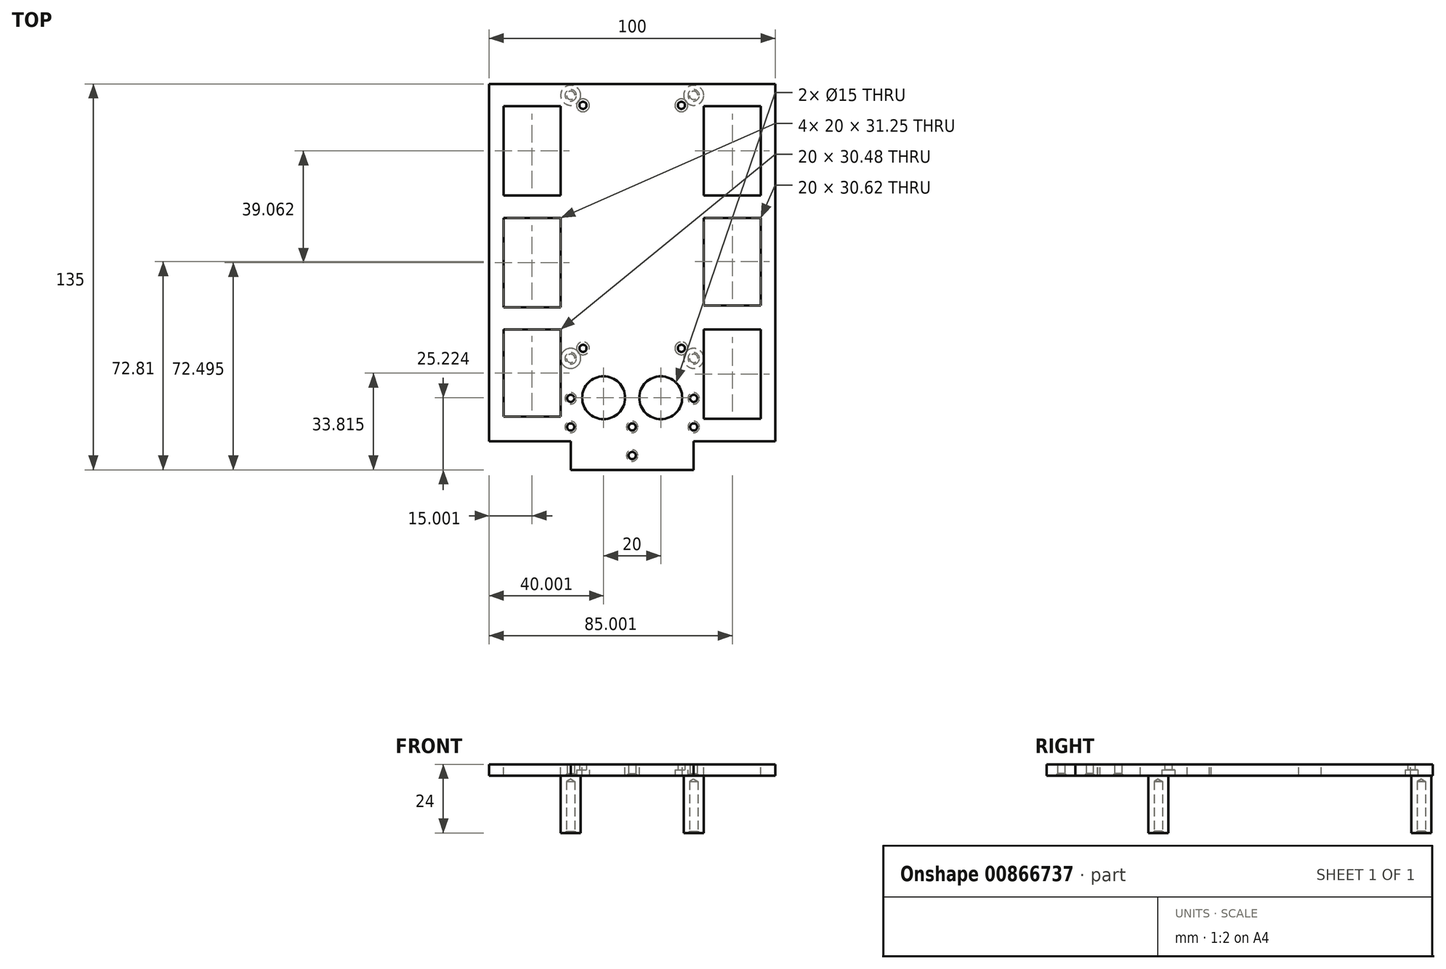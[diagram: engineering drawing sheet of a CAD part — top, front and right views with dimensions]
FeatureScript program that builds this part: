
annotation { "Feature Type Name" : "Feature", "Feature Type Description" : "" }
export const myFeature = defineFeature(function(context is Context, id is Id, definition is map)
    precondition{}
    {
        {
            assignVariable(context, id + "F0", {"name" : "RackThickness", "anyValue" : 4});
        }
        {
            assignVariable(context, id + "F1", {"name" : "PillarHeight", "anyValue" : 20});
        }
        {
            assignVariable(context, id + "F2", {"name" : "TailExtension", "anyValue" : 25});
        }
        {
            assignVariable(context, id + "F3", {"name" : "RackWidthExtension", "anyValue" : 25});
        }
        {
            var Q0;
            Q0=qCreatedBy(makeId("Top.planeOp"),FACE);
            var sketch = newSketch(context, id + "F4", { "sketchPlane" : qUnion([Q0])});
            skLineSegment(sketch, "E0.bottom", {"start": v(-22.43, 77.5) * mm, "end": v(27.57, 77.5) * mm});
            skLineSegment(sketch, "E0.top", {"start": v(-22.43, -22.5) * mm, "end": v(27.57, -22.5) * mm});
            skLineSegment(sketch, "E0.left", {"start": v(-22.43, 77.5) * mm, "end": v(-22.43, -22.5) * mm});
            skLineSegment(sketch, "E0.right", {"start": v(27.57, 77.5) * mm, "end": v(27.57, -22.5) * mm});
            skPoint(sketch, "E1", {"position": v(-14.63, 70) * mm});
            skPoint(sketch, "E2", {"position": v(19.77, 70) * mm});
            skPoint(sketch, "E3", {"position": v(19.77, -15) * mm});
            skPoint(sketch, "E4", {"position": v(-14.63, -15) * mm});
            skPoint(sketch, "E5", {"position": v(-18.93, -18.5) * mm});
            skPoint(sketch, "E6", {"position": v(24.07, -18.5) * mm});
            skPoint(sketch, "E7", {"position": v(24.07, 73.5) * mm});
            skPoint(sketch, "E8", {"position": v(-18.93, 73.5) * mm});
            skCircle(sketch, "E9", {"center": v(-18.93, 73.5) * mm, "radius": 3.5 * mm});
            skCircle(sketch, "E10", {"center": v(-18.93, -18.5) * mm, "radius": 3.5 * mm});
            skCircle(sketch, "E11", {"center": v(24.07, -18.5) * mm, "radius": 3.5 * mm});
            skCircle(sketch, "E12", {"center": v(24.07, 73.5) * mm, "radius": 3.5 * mm});
            skSolve(sketch);
        }
        {
            var Q0;
            Q0=makeQuery(id+"F4.imprint","IMPRINT",FACE,{"disambiguationData":[TD([[makeQuery(id+"F4.imprint","IMPRINT",EDGE,{"derivedFrom":sQuery(id+"F4.wireOp",EDGE,"E0.bottom")}),-1.0]])]});
            var Q1;
            Q1=makeQuery(id+"F4.imprint","IMPRINT",FACE,{"disambiguationData":[TD([[makeQuery(id+"F4.imprint","IMPRINT",EDGE,{"derivedFrom":sQuery(id+"F4.wireOp",EDGE,"E10")}),1.0]])]});
            var Q2;
            Q2=makeQuery(id+"F4.imprint","IMPRINT",FACE,{"disambiguationData":[TD([[makeQuery(id+"F4.imprint","IMPRINT",EDGE,{"derivedFrom":sQuery(id+"F4.wireOp",EDGE,"E11")}),1.0]])]});
            var Q3;
            Q3=makeQuery(id+"F4.imprint","IMPRINT",FACE,{"disambiguationData":[TD([[makeQuery(id+"F4.imprint","IMPRINT",EDGE,{"derivedFrom":sQuery(id+"F4.wireOp",EDGE,"E9")}),1.0]])]});
            var Q4;
            Q4=makeQuery(id+"F4.imprint","IMPRINT",FACE,{"disambiguationData":[TD([[makeQuery(id+"F4.imprint","IMPRINT",EDGE,{"derivedFrom":sQuery(id+"F4.wireOp",EDGE,"E12")}),1.0]])]});
            extrude(context, id + "F5", {"entities" : qUnion([Q0, Q1, Q2, Q3, Q4]), "depth" : (getVariable(context, 'RackThickness')) * mm, "offsetDistance" : 25 * mm});
        }
        {
            var Q0;
            Q0=sQuery(id+"F4.wireOp",VERTEX,"E2");
            var Q1;
            Q1=sQuery(id+"F4.wireOp",VERTEX,"E3");
            var Q2;
            Q2=sQuery(id+"F4.wireOp",VERTEX,"E4");
            var Q3;
            Q3=sQuery(id+"F4.wireOp",VERTEX,"E1");
            var Q4;
            Q4=makeQuery(id+"F5.opExtrude","SWEPT_BODY",BODY,{"disambiguationData":[OSD([sQuery(id+"F4.wireOp",EDGE,"E0.bottom"),sQuery(id+"F4.wireOp",EDGE,"E0.top"),sQuery(id+"F4.wireOp",EDGE,"E0.left"),sQuery(id+"F4.wireOp",EDGE,"E0.right")])]});
            hole(context, id + "F6", {"style" : HoleStyle.C_BORE, "endStyle" : HoleEndStyle.THROUGH, "oppositeDirection" : true, "holeDiameter" : 2.5 * mm, "cBoreDiameter" : 4.5 * mm, "cBoreDepth" : 2 * mm, "majorDiameter" : 5 * mm, "isTappedThrough" : true, "tappedDepth" : 12 * mm, "tapClearance" : 3, "startFromSketch" : true, "locations" : qUnion([Q0, Q1, Q2, Q3]), "scope" : qUnion([Q4])});
        }
        {
            var Q0;
            Q0=makeQuery(id+"F4.imprint","IMPRINT",FACE,{"disambiguationData":[TD([[makeQuery(id+"F4.imprint","IMPRINT",EDGE,{"derivedFrom":sQuery(id+"F4.wireOp",EDGE,"E10")}),1.0]])]});
            var Q1;
            Q1=makeQuery(id+"F4.imprint","IMPRINT",FACE,{"disambiguationData":[TD([[makeQuery(id+"F4.imprint","IMPRINT",EDGE,{"derivedFrom":sQuery(id+"F4.wireOp",EDGE,"E11")}),1.0]])]});
            var Q2;
            Q2=makeQuery(id+"F4.imprint","IMPRINT",FACE,{"disambiguationData":[TD([[makeQuery(id+"F4.imprint","IMPRINT",EDGE,{"derivedFrom":sQuery(id+"F4.wireOp",EDGE,"E9")}),1.0]])]});
            var Q3;
            Q3=makeQuery(id+"F4.imprint","IMPRINT",FACE,{"disambiguationData":[TD([[makeQuery(id+"F4.imprint","IMPRINT",EDGE,{"derivedFrom":sQuery(id+"F4.wireOp",EDGE,"E12")}),1.0]])]});
            extrude(context, id + "F7", {"entities" : qUnion([Q0, Q1, Q2, Q3]), "operationType" : NewBodyOperationType.ADD, "oppositeDirection" : true, "depth" : (getVariable(context, 'PillarHeight')) * mm, "offsetDistance" : 25 * mm});
        }
        {
            var Q0;
            Q0=makeQuery(id+"F7.opExtrude","CAP_FACE",FACE,{"disambiguationData":[OSD([sQuery(id+"F4.wireOp",EDGE,"E9")])],"isStart":false});
            var sketch = newSketch(context, id + "F8", { "sketchPlane" : qUnion([Q0])});
            skPoint(sketch, "E13", {"position": v(-18.93, -73.5) * mm});
            skSolve(sketch);
        }
        {
            var Q0;
            Q0=sQuery(id+"F8.wireOp",VERTEX,"E13");
            var Q1;
            Q1=makeQuery(id+"F5.opExtrude","SWEPT_BODY",BODY,{"disambiguationData":[OSD([sQuery(id+"F4.wireOp",EDGE,"E0.bottom"),sQuery(id+"F4.wireOp",EDGE,"E0.top"),sQuery(id+"F4.wireOp",EDGE,"E0.left"),sQuery(id+"F4.wireOp",EDGE,"E0.right")])]});
            hole(context, id + "F9", {"style" : HoleStyle.C_SINK, "endStyle" : HoleEndStyle.BLIND, "holeDiameter" : 2.9 * mm, "cSinkDiameter" : 4 * mm, "cSinkAngle" : 90 * degree, "majorDiameter" : 5 * mm, "holeDepth" : (.9 * getVariable(context, 'PillarHeight')) * mm, "isTappedThrough" : true, "tappedDepth" : 12 * mm, "tapClearance" : 3, "startFromSketch" : true, "locations" : qUnion([Q0]), "scope" : qUnion([Q1])});
        }
        {
            var Q0;
            Q0=makeQuery(id+"F7.opExtrude","CAP_FACE",FACE,{"disambiguationData":[OSD([sQuery(id+"F4.wireOp",EDGE,"E10")])],"isStart":false});
            var sketch = newSketch(context, id + "F10", { "sketchPlane" : qUnion([Q0])});
            skPoint(sketch, "E14", {"position": v(-18.93, 18.5) * mm});
            skSolve(sketch);
        }
        {
            var Q0;
            Q0=sQuery(id+"F10.wireOp",VERTEX,"E14");
            var Q1;
            Q1=makeQuery(id+"F5.opExtrude","SWEPT_BODY",BODY,{"disambiguationData":[OSD([sQuery(id+"F4.wireOp",EDGE,"E0.bottom"),sQuery(id+"F4.wireOp",EDGE,"E0.top"),sQuery(id+"F4.wireOp",EDGE,"E0.left"),sQuery(id+"F4.wireOp",EDGE,"E0.right")])]});
            hole(context, id + "F11", {"style" : HoleStyle.C_SINK, "endStyle" : HoleEndStyle.BLIND, "holeDiameter" : 2.9 * mm, "cSinkDiameter" : 4 * mm, "cSinkAngle" : 90 * degree, "majorDiameter" : 5 * mm, "holeDepth" : (.9 * getVariable(context, 'PillarHeight')) * mm, "isTappedThrough" : true, "tappedDepth" : 12 * mm, "tapClearance" : 3, "startFromSketch" : true, "locations" : qUnion([Q0]), "scope" : qUnion([Q1])});
        }
        {
            var Q0;
            Q0=makeQuery(id+"F7.opExtrude","CAP_FACE",FACE,{"disambiguationData":[OSD([sQuery(id+"F4.wireOp",EDGE,"E12")])],"isStart":false});
            var sketch = newSketch(context, id + "F12", { "sketchPlane" : qUnion([Q0])});
            skPoint(sketch, "E15", {"position": v(24.07, -73.5) * mm});
            skSolve(sketch);
        }
        {
            var Q0;
            Q0=sQuery(id+"F12.wireOp",VERTEX,"E15");
            var Q1;
            Q1=makeQuery(id+"F5.opExtrude","SWEPT_BODY",BODY,{"disambiguationData":[OSD([sQuery(id+"F4.wireOp",EDGE,"E0.bottom"),sQuery(id+"F4.wireOp",EDGE,"E0.top"),sQuery(id+"F4.wireOp",EDGE,"E0.left"),sQuery(id+"F4.wireOp",EDGE,"E0.right")])]});
            hole(context, id + "F13", {"style" : HoleStyle.C_SINK, "endStyle" : HoleEndStyle.BLIND, "holeDiameter" : 2.9 * mm, "cSinkDiameter" : 4 * mm, "cSinkAngle" : 90 * degree, "majorDiameter" : 5 * mm, "holeDepth" : (.9 * getVariable(context, 'PillarHeight')) * mm, "isTappedThrough" : true, "tappedDepth" : 12 * mm, "tapClearance" : 3, "startFromSketch" : true, "locations" : qUnion([Q0]), "scope" : qUnion([Q1])});
        }
        {
            var Q0;
            Q0=makeQuery(id+"F7.opExtrude","CAP_FACE",FACE,{"disambiguationData":[OSD([sQuery(id+"F4.wireOp",EDGE,"E11")])],"isStart":false});
            var sketch = newSketch(context, id + "F14", { "sketchPlane" : qUnion([Q0])});
            skPoint(sketch, "E16", {"position": v(24.07, 18.5) * mm});
            skSolve(sketch);
        }
        {
            var Q0;
            Q0=sQuery(id+"F14.wireOp",VERTEX,"E16");
            var Q1;
            Q1=makeQuery(id+"F5.opExtrude","SWEPT_BODY",BODY,{"disambiguationData":[OSD([sQuery(id+"F4.wireOp",EDGE,"E0.bottom"),sQuery(id+"F4.wireOp",EDGE,"E0.top"),sQuery(id+"F4.wireOp",EDGE,"E0.left"),sQuery(id+"F4.wireOp",EDGE,"E0.right")])]});
            hole(context, id + "F15", {"style" : HoleStyle.C_SINK, "endStyle" : HoleEndStyle.BLIND, "holeDiameter" : 2.9 * mm, "cSinkDiameter" : 4 * mm, "cSinkAngle" : 90 * degree, "majorDiameter" : 5 * mm, "holeDepth" : (.9 * getVariable(context, 'PillarHeight')) * mm, "isTappedThrough" : true, "tappedDepth" : 12 * mm, "tapClearance" : 3, "startFromSketch" : true, "locations" : qUnion([Q0]), "scope" : qUnion([Q1])});
        }
        {
            var Q0;
            Q0=makeQuery(id+"F5.opExtrude","SWEPT_FACE",FACE,{"disambiguationData":[OSD([sQuery(id+"F4.wireOp",EDGE,"E0.top")])]});
            extrude(context, id + "F16", {"entities" : qUnion([Q0]), "operationType" : NewBodyOperationType.ADD, "depth" : (getVariable(context, 'TailExtension')) * mm, "offsetDistance" : 25 * mm});
        }
        {
            var Q0;
            {var subQ0=sQuery(id+"F4.wireOp",EDGE,"E0.top");Q0=makeQuery(id+"F16.boolean.opBoolean","MERGE",FACE,{"derivedFrom":[makeQuery(id+"F5.opExtrude","CAP_FACE",FACE,{"disambiguationData":[OSD([sQuery(id+"F4.wireOp",EDGE,"E0.bottom"),subQ0,sQuery(id+"F4.wireOp",EDGE,"E0.left"),sQuery(id+"F4.wireOp",EDGE,"E0.right")])],"isStart":false}),makeQuery(id+"F16.opExtrude","SWEPT_FACE",FACE,{"disambiguationData":[OSD([subQ0]),TDD([makeQuery(id+"F5.opExtrude","CAP_EDGE",EDGE,{"disambiguationData":[OSD([subQ0])],"isStart":false})])]})]});}
            var sketch = newSketch(context, id + "F17", { "sketchPlane" : qUnion([Q0])});
            skLineSegment(sketch, "E17.bottom", {"start": v(22.57, -42.5) * mm, "end": v(-17.43, -42.5) * mm});
            skLineSegment(sketch, "E17.top", {"start": v(22.57, -22.05) * mm, "end": v(-17.43, -22.05) * mm});
            skLineSegment(sketch, "E17.left", {"start": v(22.57, -42.5) * mm, "end": v(22.57, -22.05) * mm});
            skLineSegment(sketch, "E17.right", {"start": v(-17.43, -42.5) * mm, "end": v(-17.43, -22.05) * mm});
            skPoint(sketch, "E18", {"position": v(2.57, -47.5) * mm});
            skPoint(sketch, "E19", {"position": v(2.57, -42.5) * mm});
            skLineSegment(sketch, "E20", {"start": v(2.57, -47.5) * mm, "end": v(2.57, -42.5) * mm});
            skPoint(sketch, "E21", {"position": v(2.57, -45) * mm});
            skCircle(sketch, "E22", {"center": v(2.57, -45) * mm, "radius": 1.25 * mm});
            skPoint(sketch, "E23", {"position": v(2.57, -22.05) * mm});
            skLineSegment(sketch, "E24", {"start": v(2.57, -22.05) * mm, "end": v(2.57, -42.5) * mm, "construction": true});
            skPoint(sketch, "E25", {"position": v(2.57, -32.28) * mm});
            skPoint(sketch, "E26", {"position": v(22.57, -32.28) * mm});
            skPoint(sketch, "E27", {"position": v(-17.43, -32.28) * mm});
            skLineSegment(sketch, "E28", {"start": v(22.57, -32.28) * mm, "end": v(2.57, -32.28) * mm, "construction": true});
            skPoint(sketch, "E29", {"position": v(12.57, -32.28) * mm});
            skLineSegment(sketch, "E30", {"start": v(2.57, -32.28) * mm, "end": v(-17.43, -32.28) * mm, "construction": true});
            skPoint(sketch, "E31", {"position": v(-7.43, -32.28) * mm});
            skCircle(sketch, "E32", {"center": v(12.57, -32.28) * mm, "radius": 7.5 * mm});
            skCircle(sketch, "E33", {"center": v(-7.43, -32.28) * mm, "radius": 7.5 * mm});
            skSolve(sketch);
        }
        {
            var Q0;
            {var subQ0=sQuery(id+"F4.wireOp",EDGE,"E0.right");Q0=makeQuery(id+"F16.boolean.opBoolean","MERGE",FACE,{"derivedFrom":[makeQuery(id+"F5.opExtrude","SWEPT_FACE",FACE,{"disambiguationData":[OSD([subQ0])]}),makeQuery(id+"F16.opExtrude","SWEPT_FACE",FACE,{"disambiguationData":[OSD([sQuery(id+"F4.wireOp",EDGE,"E0.top"),subQ0])]})]});}
            extrude(context, id + "F18", {"entities" : qUnion([Q0]), "operationType" : NewBodyOperationType.ADD, "depth" : (getVariable(context, 'RackWidthExtension')) * mm, "offsetDistance" : 25 * mm});
        }
        {
            var Q0;
            {var subQ0=sQuery(id+"F4.wireOp",EDGE,"E0.left");Q0=makeQuery(id+"F16.boolean.opBoolean","MERGE",FACE,{"derivedFrom":[makeQuery(id+"F5.opExtrude","SWEPT_FACE",FACE,{"disambiguationData":[OSD([subQ0])]}),makeQuery(id+"F16.opExtrude","SWEPT_FACE",FACE,{"disambiguationData":[OSD([sQuery(id+"F4.wireOp",EDGE,"E0.top"),subQ0])]})]});}
            extrude(context, id + "F19", {"entities" : qUnion([Q0]), "operationType" : NewBodyOperationType.ADD, "depth" : (getVariable(context, 'RackWidthExtension')) * mm, "offsetDistance" : 25 * mm});
        }
        {
            var Q0;
            {var subQ0=sQuery(id+"F4.wireOp",EDGE,"E0.left");var subQ1=sQuery(id+"F4.wireOp",EDGE,"E0.top");var subQ2=sQuery(id+"F4.wireOp",EDGE,"E0.right");Q0=makeQuery(id+"F19.boolean.opBoolean","MERGE",FACE,{"derivedFrom":[makeQuery(id+"F18.boolean.opBoolean","MERGE",FACE,{"derivedFrom":[makeQuery(id+"F16.boolean.opBoolean","MERGE",FACE,{"derivedFrom":[makeQuery(id+"F5.opExtrude","CAP_FACE",FACE,{"disambiguationData":[OSD([sQuery(id+"F4.wireOp",EDGE,"E0.bottom"),subQ1,subQ0,subQ2])],"isStart":false}),makeQuery(id+"F16.opExtrude","SWEPT_FACE",FACE,{"disambiguationData":[OSD([subQ1]),TDD([makeQuery(id+"F5.opExtrude","CAP_EDGE",EDGE,{"disambiguationData":[OSD([subQ1])],"isStart":false})])]})]}),makeQuery(id+"F18.opExtrude","SWEPT_FACE",FACE,{"disambiguationData":[OSD([subQ1,subQ2]),TDD([makeQuery(id+"F16.boolean.opBoolean","MERGE",EDGE,{"derivedFrom":[makeQuery(id+"F5.opExtrude","CAP_EDGE",EDGE,{"disambiguationData":[OSD([subQ2])],"isStart":false}),makeQuery(id+"F16.opExtrude","SWEPT_EDGE",EDGE,{"disambiguationData":[OSD([subQ1,subQ2]),TDD([makeQuery(id+"F5.opExtrude","CAP_VERTEX",VERTEX,{"disambiguationData":[OSD([subQ1,subQ2])],"isStart":false})])]})]})])]})]}),makeQuery(id+"F19.opExtrude","SWEPT_FACE",FACE,{"disambiguationData":[OSD([subQ1,subQ0]),TDD([makeQuery(id+"F16.boolean.opBoolean","MERGE",EDGE,{"derivedFrom":[makeQuery(id+"F5.opExtrude","CAP_EDGE",EDGE,{"disambiguationData":[OSD([subQ0])],"isStart":false}),makeQuery(id+"F16.opExtrude","SWEPT_EDGE",EDGE,{"disambiguationData":[OSD([subQ1,subQ0]),TDD([makeQuery(id+"F5.opExtrude","CAP_VERTEX",VERTEX,{"disambiguationData":[OSD([subQ1,subQ0])],"isStart":false})])]})]})])]})]});}
            var sketch = newSketch(context, id + "F20", { "sketchPlane" : qUnion([Q0])});
            skLineSegment(sketch, "E34.bottom", {"start": v(-42.43, 69.68) * mm, "end": v(-22.43, 69.68) * mm});
            skLineSegment(sketch, "E34.top", {"start": v(-42.43, 38.43) * mm, "end": v(-22.43, 38.43) * mm});
            skLineSegment(sketch, "E34.left", {"start": v(-42.43, 69.68) * mm, "end": v(-42.43, 38.43) * mm});
            skLineSegment(sketch, "E34.right", {"start": v(-22.43, 69.68) * mm, "end": v(-22.43, 38.43) * mm});
            skLineSegment(sketch, "E35.bottom", {"start": v(-42.43, 30.62) * mm, "end": v(-22.43, 30.62) * mm});
            skLineSegment(sketch, "E35.top", {"start": v(-42.43, -0.63) * mm, "end": v(-22.43, -0.63) * mm});
            skLineSegment(sketch, "E35.left", {"start": v(-42.43, 30.62) * mm, "end": v(-42.43, -0.63) * mm});
            skLineSegment(sketch, "E35.right", {"start": v(-22.43, 30.62) * mm, "end": v(-22.43, -0.63) * mm});
            skLineSegment(sketch, "E36.bottom", {"start": v(-42.43, -8.44) * mm, "end": v(-22.43, -8.44) * mm});
            skLineSegment(sketch, "E36.top", {"start": v(-42.43, -38.93) * mm, "end": v(-22.43, -38.93) * mm});
            skLineSegment(sketch, "E36.left", {"start": v(-42.43, -8.44) * mm, "end": v(-42.43, -38.93) * mm});
            skLineSegment(sketch, "E36.right", {"start": v(-22.43, -8.44) * mm, "end": v(-22.43, -38.93) * mm});
            skLineSegment(sketch, "E37.bottom", {"start": v(47.57, 69.68) * mm, "end": v(27.57, 69.68) * mm});
            skLineSegment(sketch, "E37.top", {"start": v(47.57, 38.43) * mm, "end": v(27.57, 38.43) * mm});
            skLineSegment(sketch, "E37.left", {"start": v(47.57, 69.68) * mm, "end": v(47.57, 38.43) * mm});
            skLineSegment(sketch, "E37.right", {"start": v(27.57, 69.68) * mm, "end": v(27.57, 38.43) * mm});
            skLineSegment(sketch, "E38.bottom", {"start": v(27.57, 30.62) * mm, "end": v(47.57, 30.62) * mm});
            skLineSegment(sketch, "E38.top", {"start": v(27.57, 0) * mm, "end": v(47.57, 0) * mm});
            skLineSegment(sketch, "E38.left", {"start": v(27.57, 30.62) * mm, "end": v(27.57, 0) * mm});
            skLineSegment(sketch, "E38.right", {"start": v(47.57, 30.62) * mm, "end": v(47.57, 0) * mm});
            skLineSegment(sketch, "E39.bottom", {"start": v(27.57, -8.44) * mm, "end": v(47.57, -8.44) * mm});
            skLineSegment(sketch, "E39.top", {"start": v(27.57, -39.7) * mm, "end": v(47.57, -39.7) * mm});
            skLineSegment(sketch, "E39.left", {"start": v(27.57, -8.44) * mm, "end": v(27.57, -39.7) * mm});
            skLineSegment(sketch, "E39.right", {"start": v(47.57, -8.44) * mm, "end": v(47.57, -39.7) * mm});
            skSolve(sketch);
        }
        {
            var Q0;
            Q0=makeQuery(id+"F20.imprint","IMPRINT",FACE,{"disambiguationData":[TD([[makeQuery(id+"F20.imprint","IMPRINT",EDGE,{"derivedFrom":sQuery(id+"F20.wireOp",EDGE,"E36.bottom")}),-1.0]])]});
            var Q1;
            Q1=makeQuery(id+"F20.imprint","IMPRINT",FACE,{"disambiguationData":[TD([[makeQuery(id+"F20.imprint","IMPRINT",EDGE,{"derivedFrom":sQuery(id+"F20.wireOp",EDGE,"E35.bottom")}),-1.0]])]});
            var Q2;
            Q2=makeQuery(id+"F20.imprint","IMPRINT",FACE,{"disambiguationData":[TD([[makeQuery(id+"F20.imprint","IMPRINT",EDGE,{"derivedFrom":sQuery(id+"F20.wireOp",EDGE,"E34.bottom")}),-1.0]])]});
            var Q3;
            Q3=makeQuery(id+"F20.imprint","IMPRINT",FACE,{"disambiguationData":[TD([[makeQuery(id+"F20.imprint","IMPRINT",EDGE,{"derivedFrom":sQuery(id+"F20.wireOp",EDGE,"E37.bottom")}),1.0]])]});
            var Q4;
            Q4=makeQuery(id+"F20.imprint","IMPRINT",FACE,{"disambiguationData":[TD([[makeQuery(id+"F20.imprint","IMPRINT",EDGE,{"derivedFrom":sQuery(id+"F20.wireOp",EDGE,"E38.bottom")}),-1.0]])]});
            var Q5;
            Q5=makeQuery(id+"F20.imprint","IMPRINT",FACE,{"disambiguationData":[TD([[makeQuery(id+"F20.imprint","IMPRINT",EDGE,{"derivedFrom":sQuery(id+"F20.wireOp",EDGE,"E39.bottom")}),-1.0]])]});
            extrude(context, id + "F21", {"entities" : qUnion([Q0, Q1, Q2, Q3, Q4, Q5]), "operationType" : NewBodyOperationType.REMOVE, "oppositeDirection" : true, "depth" : (getVariable(context, 'RackThickness')) * mm, "offsetDistance" : 25 * mm});
        }
        {
            var Q0;
            Q0=makeQuery(id+"F17.imprint","IMPRINT",FACE,{"disambiguationData":[TD([[makeQuery(id+"F17.imprint","IMPRINT",EDGE,{"derivedFrom":sQuery(id+"F17.wireOp",EDGE,"E33")}),1.0]])]});
            var Q1;
            Q1=makeQuery(id+"F17.imprint","IMPRINT",FACE,{"disambiguationData":[TD([[makeQuery(id+"F17.imprint","IMPRINT",EDGE,{"derivedFrom":sQuery(id+"F17.wireOp",EDGE,"E32")}),1.0]])]});
            extrude(context, id + "F22", {"entities" : qUnion([Q0, Q1]), "operationType" : NewBodyOperationType.REMOVE, "oppositeDirection" : true, "depth" : (getVariable(context, 'RackThickness')) * mm, "offsetDistance" : 25 * mm});
        }
        {
            var Q0;
            {var subQ0=sQuery(id+"F4.wireOp",EDGE,"E0.left");var subQ1=sQuery(id+"F4.wireOp",EDGE,"E0.top");var subQ2=sQuery(id+"F4.wireOp",EDGE,"E0.right");Q0=makeQuery(id+"F19.boolean.opBoolean","MERGE",FACE,{"derivedFrom":[makeQuery(id+"F18.boolean.opBoolean","MERGE",FACE,{"derivedFrom":[makeQuery(id+"F16.opExtrude","CAP_FACE",FACE,{"disambiguationData":[OSD([subQ1])],"isStart":false}),makeQuery(id+"F18.opExtrude","SWEPT_FACE",FACE,{"disambiguationData":[OSD([subQ1,subQ2]),TDD([makeQuery(id+"F16.opExtrude","CAP_EDGE",EDGE,{"disambiguationData":[OSD([subQ1,subQ2])],"isStart":false})])]})]}),makeQuery(id+"F19.opExtrude","SWEPT_FACE",FACE,{"disambiguationData":[OSD([subQ1,subQ0]),TDD([makeQuery(id+"F16.opExtrude","CAP_EDGE",EDGE,{"disambiguationData":[OSD([subQ1,subQ0])],"isStart":false})])]})]});}
            var sketch = newSketch(context, id + "F23", { "sketchPlane" : qUnion([Q0])});
            skPoint(sketch, "E40", {"position": v(2.57, 4) * mm});
            skPoint(sketch, "E41", {"position": v(2.57, 0) * mm});
            skLineSegment(sketch, "E42", {"start": v(2.57, 4) * mm, "end": v(2.57, 0) * mm, "construction": true});
            skPoint(sketch, "E43", {"position": v(2.57, 2) * mm});
            skLineSegment(sketch, "E44.bottom", {"start": v(24.07, 0) * mm, "end": v(-18.93, 0) * mm, "construction": true});
            skLineSegment(sketch, "E44.top", {"start": v(24.07, 4) * mm, "end": v(-18.93, 4) * mm, "construction": true});
            skLineSegment(sketch, "E44.left", {"start": v(24.07, 0) * mm, "end": v(24.07, 4) * mm, "construction": true});
            skLineSegment(sketch, "E44.right", {"start": v(-18.93, 0) * mm, "end": v(-18.93, 4) * mm, "construction": true});
            skLineSegment(sketch, "E45.bottom", {"start": v(24.07, 4) * mm, "end": v(-18.93, 4) * mm});
            skLineSegment(sketch, "E45.top", {"start": v(24.07, 0) * mm, "end": v(-18.93, 0) * mm});
            skLineSegment(sketch, "E45.left", {"start": v(24.07, 4) * mm, "end": v(24.07, 0) * mm});
            skLineSegment(sketch, "E45.right", {"start": v(-18.93, 4) * mm, "end": v(-18.93, 0) * mm});
            skSolve(sketch);
        }
        {
            var Q0;
            Q0=makeQuery(id+"F23.imprint","IMPRINT",FACE,{"disambiguationData":[TD([[makeQuery(id+"F23.imprint","IMPRINT",EDGE,{"derivedFrom":sQuery(id+"F23.wireOp",EDGE,"E45.bottom")}),-1.0]])]});
            extrude(context, id + "F24", {"entities" : qUnion([Q0]), "operationType" : NewBodyOperationType.ADD, "depth" : 10 * mm, "offsetDistance" : 25 * mm});
        }
        {
            var Q0;
            {var subQ0=sQuery(id+"F4.wireOp",EDGE,"E0.left");var subQ1=sQuery(id+"F4.wireOp",EDGE,"E0.top");var subQ2=sQuery(id+"F4.wireOp",EDGE,"E0.right");var subQ3=sQuery(id+"F4.wireOp",EDGE,"E0.bottom");var subQ4=makeQuery(id+"F5.opExtrude","CAP_FACE",FACE,{"disambiguationData":[OSD([subQ3,subQ1,subQ0,subQ2])],"isStart":true});var subQ5=makeQuery(id+"F5.opExtrude","SWEPT_FACE",FACE,{"disambiguationData":[OSD([subQ1])]});var subQ6=makeQuery(id+"F5.opExtrude","SWEPT_FACE",FACE,{"disambiguationData":[OSD([subQ0])]});var subQ7=makeQuery(id+"F7.opExtrude","SWEPT_FACE",FACE,{"disambiguationData":[OSD([sQuery(id+"F4.wireOp",EDGE,"E10")])]});var subQ8=makeQuery(id+"F5.opExtrude","CAP_EDGE",EDGE,{"disambiguationData":[OSD([subQ0])],"isStart":true});var subQ9=makeQuery(id+"F7.opExtrude","SWEPT_FACE",FACE,{"disambiguationData":[OSD([sQuery(id+"F4.wireOp",EDGE,"E9")])]});var subQ10=makeQuery(id+"F5.opExtrude","SWEPT_FACE",FACE,{"disambiguationData":[OSD([subQ3])]});var subQ11=makeQuery(id+"F5.opExtrude","SWEPT_FACE",FACE,{"disambiguationData":[OSD([subQ2])]});var subQ12=makeQuery(id+"F7.opExtrude","SWEPT_FACE",FACE,{"disambiguationData":[OSD([sQuery(id+"F4.wireOp",EDGE,"E11")])]});var subQ13=makeQuery(id+"F5.opExtrude","CAP_EDGE",EDGE,{"disambiguationData":[OSD([subQ2])],"isStart":true});var subQ14=makeQuery(id+"F7.opExtrude","SWEPT_FACE",FACE,{"disambiguationData":[OSD([sQuery(id+"F4.wireOp",EDGE,"E12")])]});Q0=makeQuery(id+"F24.boolean.opBoolean","MERGE",FACE,{"derivedFrom":[makeQuery(id+"F19.boolean.opBoolean","MERGE",FACE,{"derivedFrom":[makeQuery(id+"F18.boolean.opBoolean","MERGE",FACE,{"derivedFrom":[makeQuery(id+"F16.boolean.opBoolean","MERGE",FACE,{"derivedFrom":[subQ4,makeQuery(id+"F16.opExtrude","SWEPT_FACE",FACE,{"disambiguationData":[OSD([subQ1]),TDD([makeQuery(id+"F5.opExtrude","CAP_EDGE",EDGE,{"disambiguationData":[OSD([subQ1])],"isStart":true})])]})]}),makeQuery(id+"F18.opExtrude","SWEPT_FACE",FACE,{"disambiguationData":[OSD([subQ1,subQ2]),TDD([makeQuery(id+"F7.boolean.opBoolean","SPLIT",EDGE,{"disambiguationData":[TD([subQ10,subQ4,subQ11,subQ14])],"derivedFrom":subQ13}),makeQuery(id+"F7.boolean.opBoolean","SPLIT",EDGE,{"disambiguationData":[TD([subQ4,subQ11,subQ12,subQ14])],"derivedFrom":subQ13}),makeQuery(id+"F16.boolean.opBoolean","MERGE",EDGE,{"derivedFrom":[makeQuery(id+"F7.boolean.opBoolean","SPLIT",EDGE,{"disambiguationData":[TD([subQ4,subQ5,subQ11,subQ12])],"derivedFrom":subQ13}),makeQuery(id+"F16.opExtrude","SWEPT_EDGE",EDGE,{"disambiguationData":[OSD([subQ1,subQ2]),TDD([makeQuery(id+"F5.opExtrude","CAP_VERTEX",VERTEX,{"disambiguationData":[OSD([subQ1,subQ2])],"isStart":true})])]})]})])]})]}),makeQuery(id+"F19.opExtrude","SWEPT_FACE",FACE,{"disambiguationData":[OSD([subQ1,subQ0]),TDD([makeQuery(id+"F7.boolean.opBoolean","SPLIT",EDGE,{"disambiguationData":[TD([subQ10,subQ4,subQ6,subQ9])],"derivedFrom":subQ8}),makeQuery(id+"F7.boolean.opBoolean","SPLIT",EDGE,{"disambiguationData":[TD([subQ4,subQ6,subQ9,subQ7])],"derivedFrom":subQ8}),makeQuery(id+"F16.boolean.opBoolean","MERGE",EDGE,{"derivedFrom":[makeQuery(id+"F7.boolean.opBoolean","SPLIT",EDGE,{"disambiguationData":[TD([subQ4,subQ5,subQ6,subQ7])],"derivedFrom":subQ8}),makeQuery(id+"F16.opExtrude","SWEPT_EDGE",EDGE,{"disambiguationData":[OSD([subQ1,subQ0]),TDD([makeQuery(id+"F5.opExtrude","CAP_VERTEX",VERTEX,{"disambiguationData":[OSD([subQ1,subQ0])],"isStart":true})])]})]})])]})]}),makeQuery(id+"F24.opExtrude","SWEPT_FACE",FACE,{"disambiguationData":[OSD([sQuery(id+"F23.wireOp",EDGE,"E45.top")])]})]});}
            var sketch = newSketch(context, id + "F25", { "sketchPlane" : qUnion([Q0])});
            skPoint(sketch, "E46", {"position": v(2.57, 57.5) * mm});
            skPoint(sketch, "E47", {"position": v(2.57, 42.5) * mm});
            skLineSegment(sketch, "E48", {"start": v(2.57, 57.5) * mm, "end": v(2.57, 42.5) * mm});
            skPoint(sketch, "E49", {"position": v(2.57, 52.5) * mm});
            skPoint(sketch, "E50", {"position": v(2.57, 47.5) * mm});
            skLineSegment(sketch, "E51", {"start": v(-18.93, 47.5) * mm, "end": v(-18.93, 32.5) * mm});
            skLineSegment(sketch, "E52", {"start": v(-18.93, 32.5) * mm, "end": v(-18.93, 42.5) * mm});
            skLineSegment(sketch, "E53", {"start": v(24.07, 47.5) * mm, "end": v(24.07, 32.5) * mm});
            skLineSegment(sketch, "E54", {"start": v(24.07, 32.5) * mm, "end": v(24.07, 42.5) * mm});
            skSolve(sketch);
        }
        {
            var Q0;
            Q0=sQuery(id+"F25.wireOp",VERTEX,"E49");
            var Q1;
            Q1=sQuery(id+"F25.wireOp",VERTEX,"E47");
            var Q2;
            Q2=makeQuery(id+"F5.opExtrude","SWEPT_BODY",BODY,{"disambiguationData":[OSD([sQuery(id+"F4.wireOp",EDGE,"E0.bottom"),sQuery(id+"F4.wireOp",EDGE,"E0.top"),sQuery(id+"F4.wireOp",EDGE,"E0.left"),sQuery(id+"F4.wireOp",EDGE,"E0.right")])]});
            hole(context, id + "F26", {"style" : HoleStyle.C_SINK, "endStyle" : HoleEndStyle.BLIND, "holeDiameter" : 2.5 * mm, "cSinkDiameter" : 4 * mm, "cSinkAngle" : 90 * degree, "majorDiameter" : 5 * mm, "holeDepth" : 15 * mm, "isTappedThrough" : true, "tappedDepth" : 12 * mm, "tapClearance" : 3, "startFromSketch" : true, "locations" : qUnion([Q0, Q1]), "scope" : qUnion([Q2])});
        }
        {
            var Q0;
            Q0=sQuery(id+"F25.wireOp",VERTEX,"E52.end");
            var Q1;
            Q1=sQuery(id+"F25.wireOp",VERTEX,"E51.end");
            var Q2;
            Q2=sQuery(id+"F25.wireOp",VERTEX,"E53.end");
            var Q3;
            Q3=sQuery(id+"F25.wireOp",VERTEX,"E54.end");
            var Q4;
            Q4=makeQuery(id+"F5.opExtrude","SWEPT_BODY",BODY,{"disambiguationData":[OSD([sQuery(id+"F4.wireOp",EDGE,"E0.bottom"),sQuery(id+"F4.wireOp",EDGE,"E0.top"),sQuery(id+"F4.wireOp",EDGE,"E0.left"),sQuery(id+"F4.wireOp",EDGE,"E0.right")])]});
            hole(context, id + "F27", {"style" : HoleStyle.C_SINK, "endStyle" : HoleEndStyle.BLIND, "holeDiameter" : 2.5 * mm, "cSinkDiameter" : 4 * mm, "cSinkAngle" : 90 * degree, "majorDiameter" : 5 * mm, "holeDepth" : 15 * mm, "isTappedThrough" : true, "tappedDepth" : 12 * mm, "tapClearance" : 3, "startFromSketch" : true, "locations" : qUnion([Q0, Q1, Q2, Q3]), "scope" : qUnion([Q4])});
        }
    });
